FCSTD DOCUMENT  (FreeCAD 0.14R3703 (Git))
Label: 5x5 hull
License: CC-BY 3.0
LicenseURL: http://creativecommons.org/licenses/by/3.0/
objects: Sketcher::SketchObject×9
note: 9 computed .brp shape members not serialized (recipe doc carries the construction recipe); baked Part::Feature solids carry a one-line shape summary decoded from their .brp

FEATURE [Sketcher::SketchObject] Sketch  label="stemline"
  Placement = pos=(0,0,0) rot=(0.57735,0.57735,0.57735;2.0944rad)
  sketch-geometry (5):
    g0: LineSegment StartX=0 StartY=0 StartZ=0 EndX=10.8727 EndY=2.99001 EndZ=0
    g1: LineSegment StartX=10.8727 StartY=2.99001 StartZ=0 EndX=18.8611 EndY=9.19445 EndZ=0
    g2: LineSegment StartX=18.8611 StartY=9.19445 StartZ=0 EndX=24.3931 EndY=19.5304 EndZ=0
    g3: LineSegment StartX=24.3931 StartY=19.5304 StartZ=0 EndX=28.3237 EndY=28.8474 EndZ=0
    g4: LineSegment StartX=28.3237 StartY=28.8474 StartZ=0 EndX=31.2352 EndY=38.601 EndZ=0
  constraints (4):
    c: Coincident(g0,g1)
    c: Coincident(g1,g2)
    c: Coincident(g2,g3)
    c: Coincident(g3,g4)
FEATURE [Sketcher::SketchObject] Sketch001  label="cs1"
  Placement = pos=(0,0,0) rot=(1,0,0;1.5708rad)
  sketch-geometry (5):
    g0: LineSegment StartX=0 StartY=0 StartZ=0 EndX=6.25182 EndY=2.44636 EndZ=0
    g1: LineSegment StartX=6.25182 StartY=2.44636 StartZ=0 EndX=10.0573 EndY=8.15455 EndZ=0
    g2: LineSegment StartX=10.0573 StartY=8.15455 StartZ=0 EndX=12.7755 EndY=16.8527 EndZ=0
    g3: LineSegment StartX=12.7755 StartY=16.8527 StartZ=0 EndX=13.8627 EndY=25.2791 EndZ=0
    g4: LineSegment StartX=13.8627 StartY=25.2791 StartZ=0 EndX=13.8087 EndY=33.1027 EndZ=0
  constraints (4):
    c: Coincident(g0,g1)
    c: Coincident(g1,g2)
    c: Coincident(g2,g3)
    c: Coincident(g3,g4)
FEATURE [Sketcher::SketchObject] Sketch002  label="cs3"
  Placement = pos=(0,-20,0) rot=(1,0,0;1.5708rad)
  sketch-geometry (5):
    g0: LineSegment StartX=0 StartY=0 StartZ=0 EndX=7.46378 EndY=2.5553 EndZ=0
    g1: LineSegment StartX=7.46378 StartY=2.5553 StartZ=0 EndX=11.6502 EndY=7.59202 EndZ=0
    g2: LineSegment StartX=11.6502 StartY=7.59202 StartZ=0 EndX=14.6591 EndY=15.5723 EndZ=0
    g3: LineSegment StartX=14.6591 StartY=15.5723 StartZ=0 EndX=15.6403 EndY=24.2721 EndZ=0
    g4: LineSegment StartX=15.6403 StartY=24.2721 StartZ=0 EndX=15.8365 EndY=29.5051 EndZ=0
  constraints (4):
    c: Coincident(g0,g1)
    c: Coincident(g1,g2)
    c: Coincident(g2,g3)
    c: Coincident(g3,g4)
FEATURE [Sketcher::SketchObject] Sketch003  label="cs4"
  Placement = pos=(0,-40,0) rot=(1,0,0;1.5708rad)
  sketch-geometry (5):
    g0: LineSegment StartX=0 StartY=0 StartZ=0 EndX=8.15455 EndY=2.71818 EndZ=0
    g1: LineSegment StartX=8.15455 StartY=2.71818 StartZ=0 EndX=12.5036 EndY=7.61091 EndZ=0
    g2: LineSegment StartX=12.5036 StartY=7.61091 StartZ=0 EndX=15.4936 EndY=15.4936 EndZ=0
    g3: LineSegment StartX=15.4936 StartY=15.4936 StartZ=0 EndX=16.5809 EndY=24.4636 EndZ=0
    g4: LineSegment StartX=16.5809 StartY=24.4636 StartZ=0 EndX=17.1246 EndY=29.6282 EndZ=0
  constraints (4):
    c: Coincident(g0,g1)
    c: Coincident(g1,g2)
    c: Coincident(g2,g3)
    c: Coincident(g3,g4)
FEATURE [Sketcher::SketchObject] Sketch004  label="cs5"
  Placement = pos=(0,-60,0) rot=(1,0,0;1.5708rad)
  sketch-geometry (5):
    g0: LineSegment StartX=0 StartY=0 StartZ=0 EndX=8.15455 EndY=2.71818 EndZ=0
    g1: LineSegment StartX=8.15455 StartY=2.71818 StartZ=0 EndX=12.5036 EndY=7.61091 EndZ=0
    g2: LineSegment StartX=12.5036 StartY=7.61091 StartZ=0 EndX=15.4936 EndY=15.4936 EndZ=0
    g3: LineSegment StartX=15.4936 StartY=15.4936 StartZ=0 EndX=16.5809 EndY=24.4636 EndZ=0
    g4: LineSegment StartX=16.5809 StartY=24.4636 StartZ=0 EndX=17.1246 EndY=29.6282 EndZ=0
  constraints (4):
    c: Coincident(g0,g1)
    c: Coincident(g1,g2)
    c: Coincident(g2,g3)
    c: Coincident(g3,g4)
FEATURE [Sketcher::SketchObject] Sketch005  label="cs7"
  Placement = pos=(0,-80,0) rot=(1,0,0;1.5708rad)
  sketch-geometry (5):
    g0: LineSegment StartX=0 StartY=0 StartZ=0 EndX=5.86252 EndY=4.15262 EndZ=0
    g1: LineSegment StartX=5.86252 StartY=4.15262 StartZ=0 EndX=8.54951 EndY=7.69456 EndZ=0
    g2: LineSegment StartX=8.54951 StartY=7.69456 StartZ=0 EndX=11.4808 EndY=16.1219 EndZ=0
    g3: LineSegment StartX=11.4808 StartY=16.1219 StartZ=0 EndX=12.9447 EndY=24.8351 EndZ=0
    g4: LineSegment StartX=12.9447 StartY=24.8351 StartZ=0 EndX=13.0117 EndY=25.3043 EndZ=0
  constraints (4):
    c: Coincident(g0,g1)
    c: Coincident(g1,g2)
    c: Coincident(g2,g3)
    c: Coincident(g3,g4)
FEATURE [Sketcher::SketchObject] Sketch006  label="tansomXY"
  sketch-geometry (5):
    g0: LineSegment StartX=-0.075931 StartY=-89.2583 StartZ=0 EndX=3.6943 EndY=-88.5274 EndZ=0
    g1: LineSegment StartX=3.6943 StartY=-88.5274 StartZ=0 EndX=7.42606 EndY=-87.3732 EndZ=0
    g2: LineSegment StartX=7.42606 StartY=-87.3732 StartZ=0 EndX=10.2345 EndY=-85.6805 EndZ=0
    g3: LineSegment StartX=10.2345 StartY=-85.6805 StartZ=0 EndX=12.0811 EndY=-83.0644 EndZ=0
    g4: LineSegment StartX=12.0811 StartY=-83.0644 StartZ=0 EndX=12.8725 EndY=-80.086 EndZ=0
  constraints (4):
    c: Coincident(g0,g1)
    c: Coincident(g1,g2)
    c: Coincident(g2,g3)
    c: Coincident(g3,g4)
FEATURE [Sketcher::SketchObject] Sketch007  label="cs6"
  Placement = pos=(0,-65,0) rot=(1,0,0;1.5708rad)
  sketch-geometry (5):
    g0: LineSegment StartX=0 StartY=0 StartZ=0 EndX=8.13282 EndY=2.68168 EndZ=0
    g1: LineSegment StartX=8.13282 StartY=2.68168 StartZ=0 EndX=12.5868 EndY=7.6168 EndZ=0
    g2: LineSegment StartX=12.5868 StartY=7.6168 StartZ=0 EndX=15.4528 EndY=15.4022 EndZ=0
    g3: LineSegment StartX=15.4528 StartY=15.4022 StartZ=0 EndX=16.5223 EndY=24.0003 EndZ=0
    g4: LineSegment StartX=16.5223 StartY=24.0003 StartZ=0 EndX=16.5223 EndY=24.428 EndZ=0
  constraints (4):
    c: Coincident(g0,g1)
    c: Coincident(g1,g2)
    c: Coincident(g2,g3)
    c: Coincident(g3,g4)
FEATURE [Sketcher::SketchObject] Sketch008  label="cs2"
  Placement = pos=(0,-5,0) rot=(1,0,0;1.5708rad)
  sketch-geometry (5):
    g0: LineSegment StartX=0 StartY=0 StartZ=0 EndX=6.548 EndY=2.42448 EndZ=0
    g1: LineSegment StartX=6.548 StartY=2.42448 StartZ=0 EndX=10.8652 EndY=8.04992 EndZ=0
    g2: LineSegment StartX=10.8652 StartY=8.04992 StartZ=0 EndX=13.8087 EndY=16.2918 EndZ=0
    g3: LineSegment StartX=13.8087 StartY=16.2918 StartZ=0 EndX=14.7245 EndY=24.8608 EndZ=0
    g4: LineSegment StartX=14.7245 StartY=24.8608 StartZ=0 EndX=14.6591 EndY=29.5705 EndZ=0
  constraints (4):
    c: Coincident(g0,g1)
    c: Coincident(g1,g2)
    c: Coincident(g2,g3)
    c: Coincident(g3,g4)
